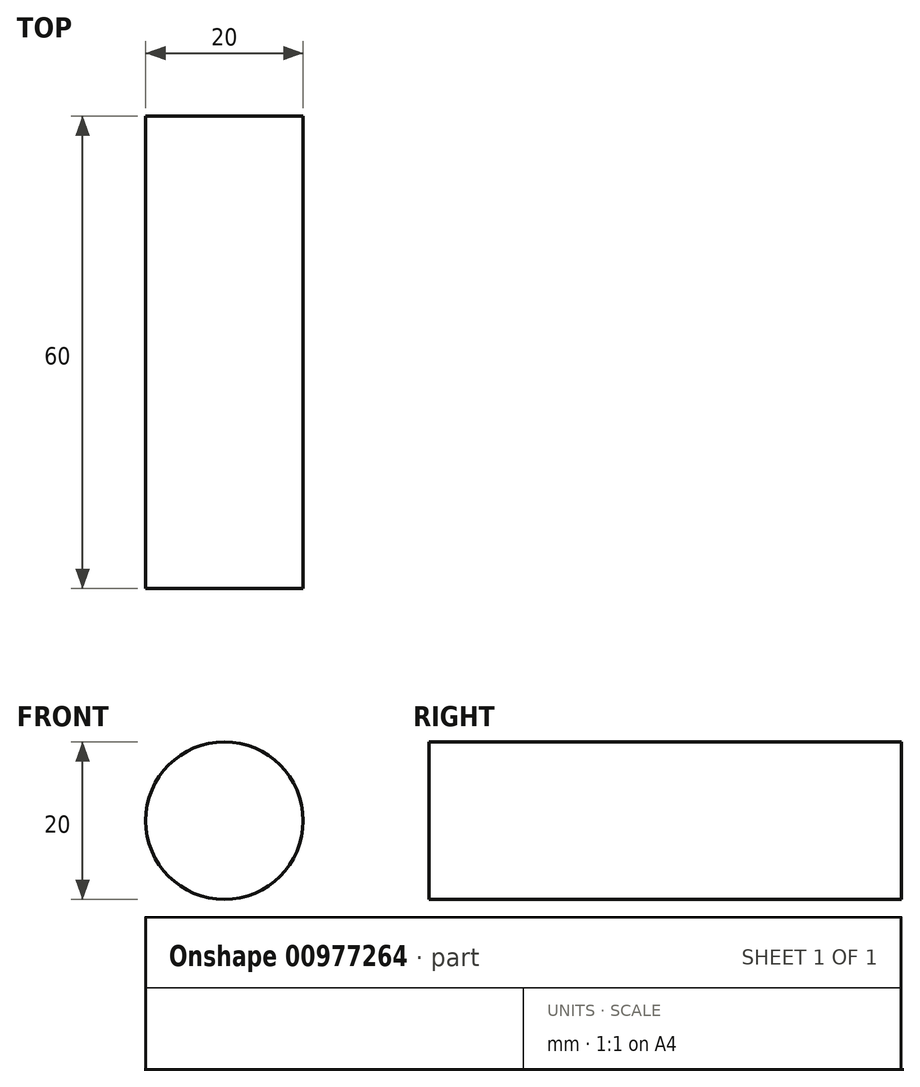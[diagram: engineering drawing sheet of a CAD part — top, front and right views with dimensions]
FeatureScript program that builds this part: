
annotation { "Feature Type Name" : "Feature", "Feature Type Description" : "" }
export const myFeature = defineFeature(function(context is Context, id is Id, definition is map)
    precondition{}
    {
        {
            var Q0;
            Q0=qCreatedBy(makeId("Front.planeOp"),FACE);
            var sketch = newSketch(context, id + "F0", { "sketchPlane" : qUnion([Q0])});
            skCircle(sketch, "E0", {"center": v(0, 0) * mm, "radius": 10 * mm});
            skSolve(sketch);
        }
        {
            var Q0;
            Q0=qSketchRegion(id+"F0",true);
            extrude(context, id + "F1", {"entities" : qUnion([Q0]), "depth" : 60 * mm, "offsetDistance" : 25 * mm});
        }
    });
